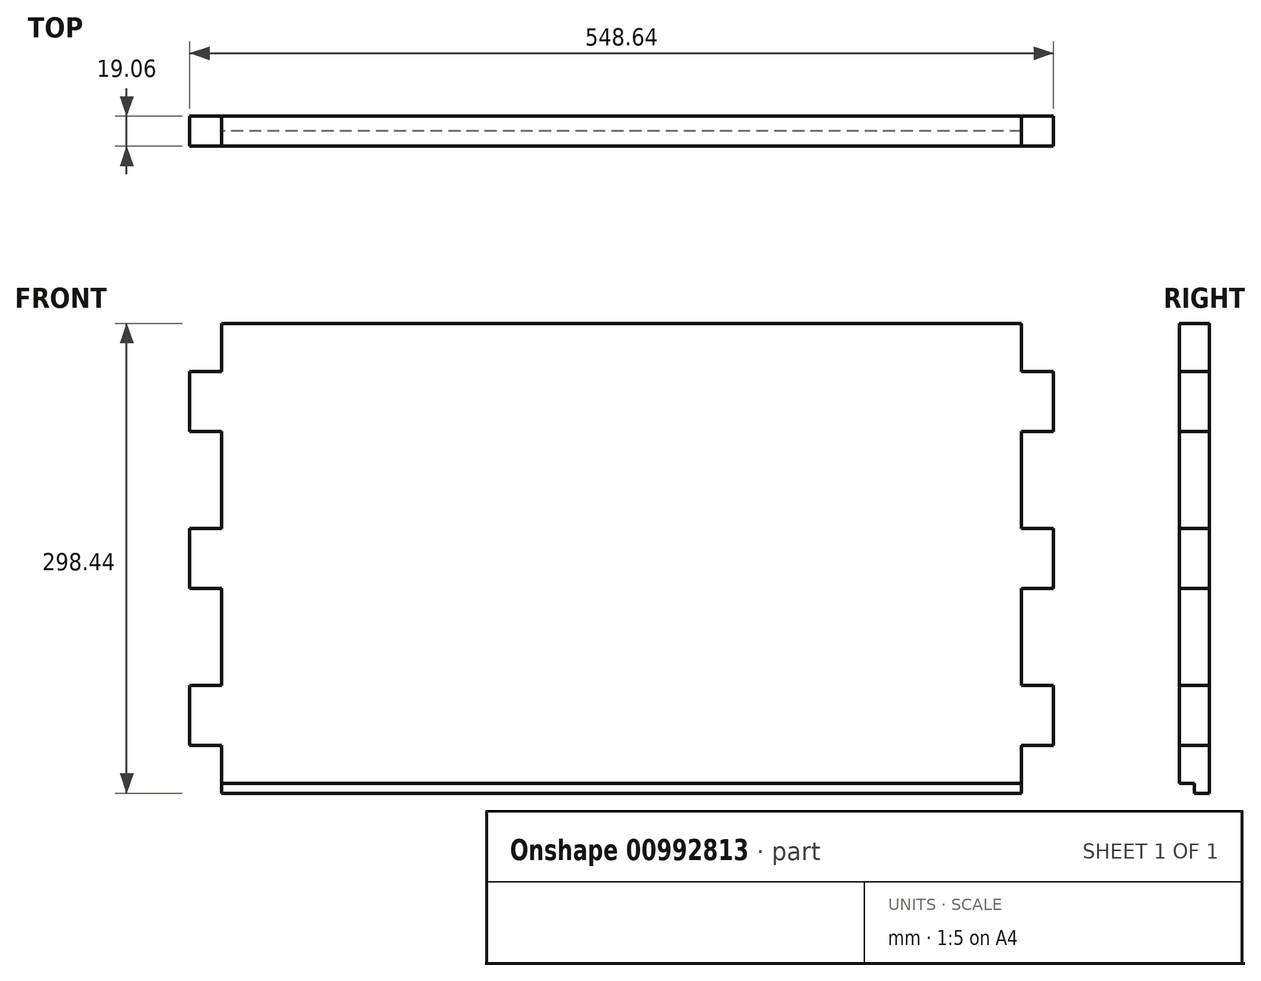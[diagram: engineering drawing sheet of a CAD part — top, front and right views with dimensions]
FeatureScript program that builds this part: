
annotation { "Feature Type Name" : "Feature", "Feature Type Description" : "" }
export const myFeature = defineFeature(function(context is Context, id is Id, definition is map)
    precondition{}
    {
        {
            var Q0;
            Q0=qCreatedBy(makeId("Front.planeOp"),FACE);
            var sketch = newSketch(context, id + "F0", { "sketchPlane" : qUnion([Q0])});
            skLineSegment(sketch, "E0", {"start": v(0, 149.22) * mm, "end": v(0, -149.23) * mm, "construction": true});
            skLineSegment(sketch, "E1", {"start": v(274.32, 0) * mm, "end": v(-274.32, 0) * mm, "construction": true});
            skLineSegment(sketch, "E2.bottom", {"start": v(-254, 149.22) * mm, "end": v(254, 149.22) * mm});
            skLineSegment(sketch, "E2.top", {"start": v(-254, -149.22) * mm, "end": v(254, -149.22) * mm});
            skLineSegment(sketch, "E2.left", {"start": v(-254, 149.22) * mm, "end": v(-254, 118.74) * mm});
            skLineSegment(sketch, "E2.right", {"start": v(254, 149.22) * mm, "end": v(254, 118.74) * mm});
            skPoint(sketch, "E2.middle", {"position": v(0, 0) * mm});
            skLineSegment(sketch, "E3.right", {"start": v(274.32, 118.74) * mm, "end": v(274.32, 80.64) * mm});
            skPoint(sketch, "E4.orphan", {"position": v(254, 0) * mm});
            skPoint(sketch, "E5.orphan", {"position": v(-254, 0) * mm});
            skLineSegment(sketch, "E6.bottom", {"start": v(254, 19.05) * mm, "end": v(274.32, 19.05) * mm});
            skLineSegment(sketch, "E6.top", {"start": v(254, 80.64) * mm, "end": v(274.32, 80.64) * mm});
            skLineSegment(sketch, "E6.left", {"start": v(254, 19.05) * mm, "end": v(254, 80.64) * mm});
            skLineSegment(sketch, "E7.bottom", {"start": v(254, 118.74) * mm, "end": v(274.32, 118.74) * mm});
            skLineSegment(sketch, "E7.left", {"start": v(254, 118.74) * mm, "end": v(254, 149.22) * mm});
            skLineSegment(sketch, "E8.bottom", {"start": v(254, -19.05) * mm, "end": v(274.32, -19.05) * mm});
            skLineSegment(sketch, "E8.top", {"start": v(254, -80.64) * mm, "end": v(274.32, -80.64) * mm});
            skLineSegment(sketch, "E8.left", {"start": v(254, -19.05) * mm, "end": v(254, -80.64) * mm});
            skLineSegment(sketch, "E9.bottom", {"start": v(254, -118.74) * mm, "end": v(274.32, -118.74) * mm});
            skLineSegment(sketch, "E10.trimOffspring", {"start": v(274.32, 19.05) * mm, "end": v(274.32, -19.05) * mm});
            skLineSegment(sketch, "E11.trimOffspring", {"start": v(274.32, -80.64) * mm, "end": v(274.32, -118.74) * mm});
            skLineSegment(sketch, "E12.MirrorCS", {"start": v(-254, -118.74) * mm, "end": v(-274.32, -118.74) * mm});
            skLineSegment(sketch, "E13.MirrorCS", {"start": v(-274.32, -80.64) * mm, "end": v(-274.32, -118.74) * mm});
            skLineSegment(sketch, "E14.MirrorCS", {"start": v(-254, -80.64) * mm, "end": v(-274.32, -80.64) * mm});
            skLineSegment(sketch, "E15.MirrorCS", {"start": v(-254, -19.05) * mm, "end": v(-274.32, -19.05) * mm});
            skLineSegment(sketch, "E16.MirrorCS", {"start": v(-274.32, 19.05) * mm, "end": v(-274.32, -19.05) * mm});
            skLineSegment(sketch, "E17.MirrorCS", {"start": v(-254, 19.05) * mm, "end": v(-274.32, 19.05) * mm});
            skLineSegment(sketch, "E18.MirrorCS", {"start": v(-254, 80.64) * mm, "end": v(-274.32, 80.64) * mm});
            skLineSegment(sketch, "E19.MirrorCS", {"start": v(-274.32, 118.74) * mm, "end": v(-274.32, 80.64) * mm});
            skLineSegment(sketch, "E20.MirrorCS", {"start": v(-254, 118.74) * mm, "end": v(-274.32, 118.74) * mm});
            skLineSegment(sketch, "E21.trimOffspring", {"start": v(-254, -118.74) * mm, "end": v(-254, -149.22) * mm});
            skLineSegment(sketch, "E22.trimOffspring", {"start": v(-254, -118.74) * mm, "end": v(-254, -149.23) * mm});
            skLineSegment(sketch, "E23.trimOffspring", {"start": v(-254, 80.64) * mm, "end": v(-254, 19.05) * mm});
            skLineSegment(sketch, "E24.trimOffspring", {"start": v(-254, -19.05) * mm, "end": v(-254, -80.64) * mm});
            skLineSegment(sketch, "E25.trimOffspring", {"start": v(254, -118.74) * mm, "end": v(254, -149.22) * mm});
            skLineSegment(sketch, "E26.trimOffspring", {"start": v(254, 80.64) * mm, "end": v(254, 19.05) * mm});
            skSolve(sketch);
        }
        {
            var Q0;
            Q0 = qSketchRegion(id + "F0", true);
            extrude(context, id + "F1", {"entities" : qUnion([Q0]), "endBound" : BoundingType.SYMMETRIC, "depth" : 19.05 * mm, "offsetDistance" : 25.4 * mm});
        }
        {
            var Q0;
            Q0=makeQuery(id+"F1.opExtrude","SWEPT_FACE",FACE,{"disambiguationData":[OSD([sQuery(id+"F0.wireOp",EDGE,"E22.trimOffspring")])]});
            var sketch = newSketch(context, id + "F2", { "sketchPlane" : qUnion([Q0])});
            skLineSegment(sketch, "E27.bottom", {"start": v(9.53, -149.22) * mm, "end": v(0, -149.22) * mm});
            skLineSegment(sketch, "E27.top", {"start": v(9.52, -142.88) * mm, "end": v(0, -142.88) * mm});
            skLineSegment(sketch, "E27.left", {"start": v(9.53, -149.22) * mm, "end": v(9.52, -142.88) * mm});
            skLineSegment(sketch, "E27.right", {"start": v(0, -149.22) * mm, "end": v(0, -142.88) * mm});
            skSolve(sketch);
        }
        {
            var Q0;
            Q0=makeQuery(id+"F2.imprint","IMPRINT",FACE,{"disambiguationData":[TD([[makeQuery(id+"F2.imprint","IMPRINT",EDGE,{"derivedFrom":sQuery(id+"F2.wireOp",EDGE,"E27.bottom")}),-1.0]])]});
            extrude(context, id + "F3", {"entities" : qUnion([Q0]), "operationType" : NewBodyOperationType.REMOVE, "endBound" : BoundingType.THROUGH_ALL, "oppositeDirection" : true, "depth" : 25.4 * mm, "offsetDistance" : 25.4 * mm});
        }
    });
